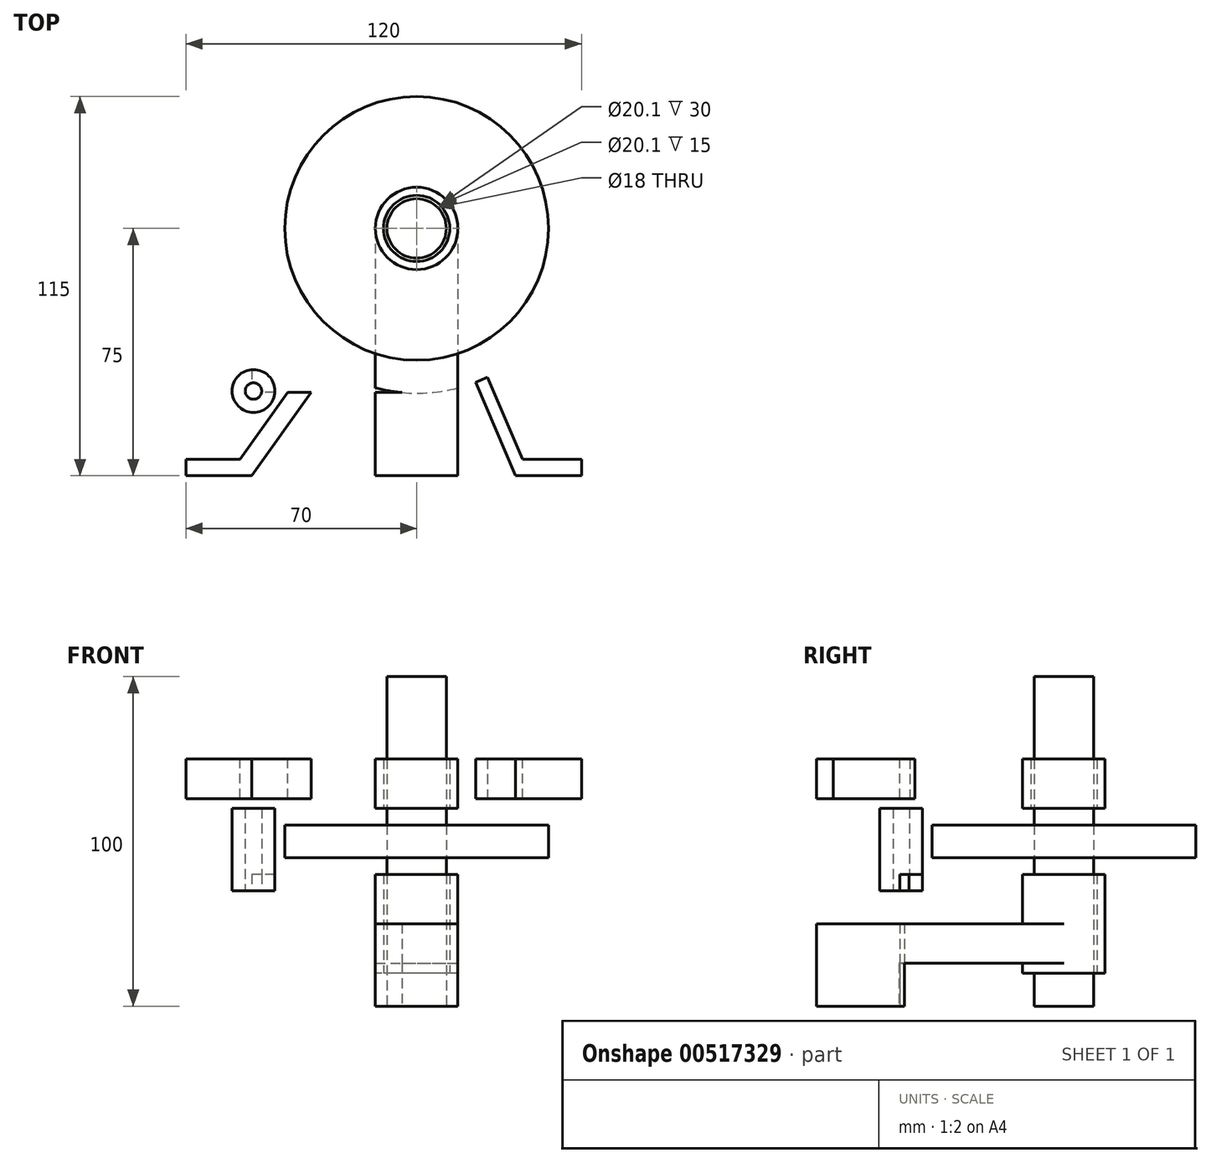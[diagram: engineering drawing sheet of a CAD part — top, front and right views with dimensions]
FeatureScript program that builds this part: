
annotation { "Feature Type Name" : "Feature", "Feature Type Description" : "" }
export const myFeature = defineFeature(function(context is Context, id is Id, definition is map)
    precondition{}
    {
        {
            var Q0;
            Q0=qCreatedBy(makeId("Top.planeOp"),FACE);
            var sketch = newSketch(context, id + "F0", { "sketchPlane" : qUnion([Q0])});
            skCircle(sketch, "E0", {"center": v(0, 0) * mm, "radius": 9 * mm});
            skCircle(sketch, "E1", {"center": v(0, 0) * mm, "radius": 10.05 * mm});
            skCircle(sketch, "E2", {"center": v(0, 0) * mm, "radius": 12.5 * mm});
            skCircle(sketch, "E3", {"center": v(0, 0) * mm, "radius": 50 * mm});
            skLineSegment(sketch, "E4", {"start": v(0, 0) * mm, "end": v(-35.84, -34.86) * mm});
            skLineSegment(sketch, "E5", {"start": v(0, 0) * mm, "end": v(0, 50) * mm});
            skCircle(sketch, "E6", {"center": v(0, 0) * mm, "radius": 45 * mm});
            skCircle(sketch, "E7", {"center": v(0, 0) * mm, "radius": 40 * mm});
            skLineSegment(sketch, "E8.bottom", {"start": v(-12.5, 75) * mm, "end": v(12.5, 75) * mm});
            skLineSegment(sketch, "E8.top", {"start": v(-12.5, -75) * mm, "end": v(12.5, -75) * mm});
            skLineSegment(sketch, "E8.left", {"start": v(-12.5, 75) * mm, "end": v(-12.5, -75) * mm});
            skLineSegment(sketch, "E8.right", {"start": v(12.5, 75) * mm, "end": v(12.5, -75) * mm});
            skLineSegment(sketch, "E9", {"start": v(-50, 0) * mm, "end": v(-50, -49.8) * mm});
            skLineSegment(sketch, "E10", {"start": v(-4.45, -49.8) * mm, "end": v(-50, -49.8) * mm});
            skSolve(sketch);
        }
        {
            var Q0;
            Q0=makeQuery(id+"F0.imprint","IMPRINT",FACE,{"disambiguationData":[TD([[makeQuery(id+"F0.imprint","IMPRINT",EDGE,{"derivedFrom":sQuery(id+"F0.wireOp",EDGE,"E0")}),1.0]])]});
            extrude(context, id + "F1", {"entities" : qUnion([Q0]), "depth" : 100 * mm, "offsetDistance" : 25 * mm});
        }
        {
            var Q0;
            {var subQ0=sQuery(id+"F0.wireOp",EDGE,"E4");var subQ1=sQuery(id+"F0.wireOp",EDGE,"E1");var subQ2=makeQuery(id+"F0.imprint","INTERSECT",VERTEX,{"derivedFrom":[subQ1,subQ0]});Q0=makeQuery(id+"F0.imprint","IMPRINT",FACE,{"disambiguationData":[TD([[makeQuery(id+"F0.imprint","IMPRINT",EDGE,{"disambiguationData":[TD([[subQ2,-1.0]])],"derivedFrom":subQ1}),-1.0]])]});}
            var Q1;
            {var subQ0=sQuery(id+"F0.wireOp",EDGE,"E4");var subQ1=sQuery(id+"F0.wireOp",EDGE,"E1");var subQ2=makeQuery(id+"F0.imprint","INTERSECT",VERTEX,{"derivedFrom":[subQ1,subQ0]});Q1=makeQuery(id+"F0.imprint","IMPRINT",FACE,{"disambiguationData":[TD([[makeQuery(id+"F0.imprint","IMPRINT",EDGE,{"disambiguationData":[TD([[subQ2,1.0]])],"derivedFrom":subQ1}),-1.0]])]});}
            extrude(context, id + "F2", {"entities" : qUnion([Q0, Q1]), "depth" : 40 * mm, "offsetDistance" : 25 * mm, "hasSecondDirection" : true, "secondDirectionOppositeDirection" : true, "secondDirectionDepth" : -10 * mm});
        }
        {
            var Q0;
            {var subQ0=sQuery(id+"F0.wireOp",EDGE,"E4");var subQ1=sQuery(id+"F0.wireOp",EDGE,"E1");var subQ2=makeQuery(id+"F0.imprint","INTERSECT",VERTEX,{"derivedFrom":[subQ1,subQ0]});Q0=makeQuery(id+"F0.imprint","IMPRINT",FACE,{"disambiguationData":[TD([[makeQuery(id+"F0.imprint","IMPRINT",EDGE,{"disambiguationData":[TD([[subQ2,-1.0]])],"derivedFrom":subQ1}),-1.0]])]});}
            var Q1;
            {var subQ0=sQuery(id+"F0.wireOp",EDGE,"E4");var subQ1=sQuery(id+"F0.wireOp",EDGE,"E1");var subQ2=makeQuery(id+"F0.imprint","INTERSECT",VERTEX,{"derivedFrom":[subQ1,subQ0]});Q1=makeQuery(id+"F0.imprint","IMPRINT",FACE,{"disambiguationData":[TD([[makeQuery(id+"F0.imprint","IMPRINT",EDGE,{"disambiguationData":[TD([[subQ2,1.0]])],"derivedFrom":subQ1}),-1.0]])]});}
            extrude(context, id + "F3", {"entities" : qUnion([Q0, Q1]), "depth" : 75 * mm, "offsetDistance" : 25 * mm, "hasSecondDirection" : true, "secondDirectionOppositeDirection" : true, "secondDirectionDepth" : -60 * mm});
        }
        {
            var Q0;
            {var subQ0=sQuery(id+"F0.wireOp",EDGE,"E4");var subQ1=sQuery(id+"F0.wireOp",EDGE,"E2");var subQ2=makeQuery(id+"F0.imprint","INTERSECT",VERTEX,{"derivedFrom":[subQ1,subQ0]});Q0=makeQuery(id+"F0.imprint","IMPRINT",FACE,{"disambiguationData":[TD([[makeQuery(id+"F0.imprint","IMPRINT",EDGE,{"disambiguationData":[TD([[subQ2,-1.0]])],"derivedFrom":subQ1}),-1.0]])]});}
            var Q1;
            {var subQ0=sQuery(id+"F0.wireOp",EDGE,"E4");var subQ1=sQuery(id+"F0.wireOp",EDGE,"E3");var subQ2=makeQuery(id+"F0.imprint","INTERSECT",VERTEX,{"derivedFrom":[subQ1,subQ0]});Q1=makeQuery(id+"F0.imprint","IMPRINT",FACE,{"disambiguationData":[TD([[makeQuery(id+"F0.imprint","IMPRINT",EDGE,{"disambiguationData":[TD([[subQ2,-1.0]])],"derivedFrom":subQ1}),1.0]])]});}
            var Q2;
            {var subQ0=sQuery(id+"F0.wireOp",EDGE,"E7");var subQ1=sQuery(id+"F0.wireOp",EDGE,"E4");var subQ2=makeQuery(id+"F0.imprint","INTERSECT",VERTEX,{"derivedFrom":[subQ1,subQ0]});Q2=makeQuery(id+"F0.imprint","IMPRINT",FACE,{"disambiguationData":[TD([[makeQuery(id+"F0.imprint","IMPRINT",EDGE,{"disambiguationData":[TD([[subQ2,-1.0]])],"derivedFrom":subQ1}),1.0]])]});}
            var Q3;
            {var subQ0=sQuery(id+"F0.wireOp",EDGE,"E7");var subQ1=sQuery(id+"F0.wireOp",EDGE,"E5");var subQ2=makeQuery(id+"F0.imprint","INTERSECT",VERTEX,{"derivedFrom":[subQ1,subQ0]});Q3=makeQuery(id+"F0.imprint","IMPRINT",FACE,{"disambiguationData":[TD([[makeQuery(id+"F0.imprint","IMPRINT",EDGE,{"disambiguationData":[TD([[subQ2,-1.0]])],"derivedFrom":subQ1}),-1.0]])]});}
            var Q4;
            {var subQ0=sQuery(id+"F0.wireOp",EDGE,"E5");var subQ1=sQuery(id+"F0.wireOp",EDGE,"E3");var subQ2=makeQuery(id+"F0.imprint","INTERSECT",VERTEX,{"derivedFrom":[subQ1,subQ0]});Q4=makeQuery(id+"F0.imprint","IMPRINT",FACE,{"disambiguationData":[TD([[makeQuery(id+"F0.imprint","IMPRINT",EDGE,{"disambiguationData":[TD([[subQ2,1.0]])],"derivedFrom":subQ1}),1.0]])]});}
            var Q5;
            {var subQ0=sQuery(id+"F0.wireOp",EDGE,"E8.right");var subQ1=sQuery(id+"F0.wireOp",EDGE,"E3");var subQ2=makeQuery(id+"F0.imprint","INTERSECT",VERTEX,{"disambiguationData":[OD(0.0)],"derivedFrom":[subQ1,subQ0]});Q5=makeQuery(id+"F0.imprint","IMPRINT",FACE,{"disambiguationData":[TD([[makeQuery(id+"F0.imprint","IMPRINT",EDGE,{"disambiguationData":[TD([[subQ2,1.0]])],"derivedFrom":subQ1}),1.0]])]});}
            var Q6;
            {var subQ0=sQuery(id+"F0.wireOp",EDGE,"E8.right");var subQ1=sQuery(id+"F0.wireOp",EDGE,"E6");var subQ2=makeQuery(id+"F0.imprint","INTERSECT",VERTEX,{"disambiguationData":[OD(0.0)],"derivedFrom":[subQ1,subQ0]});Q6=makeQuery(id+"F0.imprint","IMPRINT",FACE,{"disambiguationData":[TD([[makeQuery(id+"F0.imprint","IMPRINT",EDGE,{"disambiguationData":[TD([[subQ2,1.0]])],"derivedFrom":subQ1}),1.0]])]});}
            var Q7;
            {var subQ0=sQuery(id+"F0.wireOp",EDGE,"E8.left");var subQ1=sQuery(id+"F0.wireOp",EDGE,"E6");var subQ2=makeQuery(id+"F0.imprint","INTERSECT",VERTEX,{"disambiguationData":[OD(1.0)],"derivedFrom":[subQ1,subQ0]});Q7=makeQuery(id+"F0.imprint","IMPRINT",FACE,{"disambiguationData":[TD([[makeQuery(id+"F0.imprint","IMPRINT",EDGE,{"disambiguationData":[TD([[subQ2,-1.0]])],"derivedFrom":subQ1}),1.0]])]});}
            var Q8;
            {var subQ0=sQuery(id+"F0.wireOp",EDGE,"E8.left");var subQ1=sQuery(id+"F0.wireOp",EDGE,"E3");var subQ2=makeQuery(id+"F0.imprint","INTERSECT",VERTEX,{"disambiguationData":[OD(1.0)],"derivedFrom":[subQ1,subQ0]});Q8=makeQuery(id+"F0.imprint","IMPRINT",FACE,{"disambiguationData":[TD([[makeQuery(id+"F0.imprint","IMPRINT",EDGE,{"disambiguationData":[TD([[subQ2,-1.0]])],"derivedFrom":subQ1}),1.0]])]});}
            var Q9;
            {var subQ0=sQuery(id+"F0.wireOp",EDGE,"E8.right");var subQ1=sQuery(id+"F0.wireOp",EDGE,"E7");var subQ2=makeQuery(id+"F0.imprint","INTERSECT",VERTEX,{"disambiguationData":[OD(0.0)],"derivedFrom":[subQ1,subQ0]});Q9=makeQuery(id+"F0.imprint","IMPRINT",FACE,{"disambiguationData":[TD([[makeQuery(id+"F0.imprint","IMPRINT",EDGE,{"disambiguationData":[TD([[subQ2,1.0]])],"derivedFrom":subQ1}),1.0]])]});}
            var Q10;
            {var subQ0=sQuery(id+"F0.wireOp",EDGE,"E5");var subQ1=sQuery(id+"F0.wireOp",EDGE,"E2");var subQ2=makeQuery(id+"F0.imprint","INTERSECT",VERTEX,{"derivedFrom":[subQ1,subQ0]});Q10=makeQuery(id+"F0.imprint","IMPRINT",FACE,{"disambiguationData":[TD([[makeQuery(id+"F0.imprint","IMPRINT",EDGE,{"disambiguationData":[TD([[subQ2,1.0]])],"derivedFrom":subQ1}),-1.0]])]});}
            var Q11;
            {var subQ0=sQuery(id+"F0.wireOp",EDGE,"E8.left");var subQ1=sQuery(id+"F0.wireOp",EDGE,"E4");var subQ2=makeQuery(id+"F0.imprint","INTERSECT",VERTEX,{"derivedFrom":[subQ1,subQ0]});Q11=makeQuery(id+"F0.imprint","IMPRINT",FACE,{"disambiguationData":[TD([[makeQuery(id+"F0.imprint","IMPRINT",EDGE,{"disambiguationData":[TD([[subQ2,-1.0]])],"derivedFrom":subQ1}),1.0]])]});}
            var Q12;
            {var subQ0=sQuery(id+"F0.wireOp",EDGE,"E5");var subQ1=sQuery(id+"F0.wireOp",EDGE,"E2");var subQ2=makeQuery(id+"F0.imprint","INTERSECT",VERTEX,{"derivedFrom":[subQ1,subQ0]});Q12=makeQuery(id+"F0.imprint","IMPRINT",FACE,{"disambiguationData":[TD([[makeQuery(id+"F0.imprint","IMPRINT",EDGE,{"disambiguationData":[TD([[subQ2,-1.0]])],"derivedFrom":subQ1}),-1.0]])]});}
            var Q13;
            {var subQ0=sQuery(id+"F0.wireOp",EDGE,"E8.left");var subQ1=sQuery(id+"F0.wireOp",EDGE,"E4");var subQ2=makeQuery(id+"F0.imprint","INTERSECT",VERTEX,{"derivedFrom":[subQ1,subQ0]});Q13=makeQuery(id+"F0.imprint","IMPRINT",FACE,{"disambiguationData":[TD([[makeQuery(id+"F0.imprint","IMPRINT",EDGE,{"disambiguationData":[TD([[subQ2,-1.0]])],"derivedFrom":subQ1}),-1.0]])]});}
            var Q14;
            {var subQ0=sQuery(id+"F0.wireOp",EDGE,"E8.left");var subQ1=sQuery(id+"F0.wireOp",EDGE,"E2");var subQ2=makeQuery(id+"F0.imprint","INTERSECT",VERTEX,{"derivedFrom":[subQ1,subQ0]});Q14=makeQuery(id+"F0.imprint","IMPRINT",FACE,{"disambiguationData":[TD([[makeQuery(id+"F0.imprint","IMPRINT",EDGE,{"disambiguationData":[TD([[subQ2,-1.0]])],"derivedFrom":subQ1}),-1.0]])]});}
            var Q15;
            {var subQ0=sQuery(id+"F0.wireOp",EDGE,"E7");var subQ1=sQuery(id+"F0.wireOp",EDGE,"E4");var subQ2=makeQuery(id+"F0.imprint","INTERSECT",VERTEX,{"derivedFrom":[subQ1,subQ0]});Q15=makeQuery(id+"F0.imprint","IMPRINT",FACE,{"disambiguationData":[TD([[makeQuery(id+"F0.imprint","IMPRINT",EDGE,{"disambiguationData":[TD([[subQ2,-1.0]])],"derivedFrom":subQ1}),-1.0]])]});}
            var Q16;
            {var subQ0=sQuery(id+"F0.wireOp",EDGE,"E4");var subQ1=sQuery(id+"F0.wireOp",EDGE,"E3");var subQ2=makeQuery(id+"F0.imprint","INTERSECT",VERTEX,{"derivedFrom":[subQ1,subQ0]});Q16=makeQuery(id+"F0.imprint","IMPRINT",FACE,{"disambiguationData":[TD([[makeQuery(id+"F0.imprint","IMPRINT",EDGE,{"disambiguationData":[TD([[subQ2,1.0]])],"derivedFrom":subQ1}),1.0]])]});}
            var Q17;
            {var subQ0=sQuery(id+"F0.wireOp",EDGE,"E7");var subQ1=sQuery(id+"F0.wireOp",EDGE,"E5");var subQ2=makeQuery(id+"F0.imprint","INTERSECT",VERTEX,{"derivedFrom":[subQ1,subQ0]});Q17=makeQuery(id+"F0.imprint","IMPRINT",FACE,{"disambiguationData":[TD([[makeQuery(id+"F0.imprint","IMPRINT",EDGE,{"disambiguationData":[TD([[subQ2,-1.0]])],"derivedFrom":subQ1}),1.0]])]});}
            var Q18;
            {var subQ0=sQuery(id+"F0.wireOp",EDGE,"E5");var subQ1=sQuery(id+"F0.wireOp",EDGE,"E3");var subQ2=makeQuery(id+"F0.imprint","INTERSECT",VERTEX,{"derivedFrom":[subQ1,subQ0]});Q18=makeQuery(id+"F0.imprint","IMPRINT",FACE,{"disambiguationData":[TD([[makeQuery(id+"F0.imprint","IMPRINT",EDGE,{"disambiguationData":[TD([[subQ2,-1.0]])],"derivedFrom":subQ1}),1.0]])]});}
            var Q19;
            {var subQ0=sQuery(id+"F0.wireOp",EDGE,"FEy6LhcJ-vW1g-UwPa-rVGF-p8I0dYB5r2JZ");var subQ1=sQuery(id+"F0.wireOp",EDGE,"E3");var subQ2=makeQuery(id+"F0.imprint","INTERSECT",VERTEX,{"derivedFrom":[subQ1,subQ0]});Q19=makeQuery(id+"F0.imprint","IMPRINT",FACE,{"disambiguationData":[TD([[makeQuery(id+"F0.imprint","IMPRINT",EDGE,{"disambiguationData":[TD([[subQ2,1.0]])],"derivedFrom":subQ1}),-1.0]])]});}
            var Q20;
            {var subQ0=sQuery(id+"F0.wireOp",EDGE,"E9");Q20=makeQuery(id+"F0.imprint","IMPRINT",FACE,{"disambiguationData":[TD([[makeQuery(id+"F0.imprint","IMPRINT",EDGE,{"derivedFrom":subQ0}),1.0]])]});}
            extrude(context, id + "F4", {"entities" : qUnion([Q0, Q1, Q2, Q3, Q4, Q5, Q6, Q7, Q8, Q9, Q10, Q11, Q12, Q13, Q14, Q15, Q16, Q17, Q18, Q19, Q20]), "operationType" : NewBodyOperationType.ADD, "depth" : 40 * mm, "offsetDistance" : 25 * mm, "hasSecondDirection" : true, "secondDirectionOppositeDirection" : true, "secondDirectionDepth" : -35 * mm});
        }
        {
            var Q0;
            {var subQ0=sQuery(id+"F0.wireOp",EDGE,"E4");var subQ1=sQuery(id+"F0.wireOp",EDGE,"E3");var subQ2=makeQuery(id+"F0.imprint","INTERSECT",VERTEX,{"derivedFrom":[subQ1,subQ0]});Q0=makeQuery(id+"F0.imprint","IMPRINT",FACE,{"disambiguationData":[TD([[makeQuery(id+"F0.imprint","IMPRINT",EDGE,{"disambiguationData":[TD([[subQ2,-1.0]])],"derivedFrom":subQ1}),1.0]])]});}
            var Q1;
            {var subQ0=sQuery(id+"F0.wireOp",EDGE,"E8.left");var subQ1=sQuery(id+"F0.wireOp",EDGE,"E3");var subQ2=makeQuery(id+"F0.imprint","INTERSECT",VERTEX,{"disambiguationData":[OD(1.0)],"derivedFrom":[subQ1,subQ0]});Q1=makeQuery(id+"F0.imprint","IMPRINT",FACE,{"disambiguationData":[TD([[makeQuery(id+"F0.imprint","IMPRINT",EDGE,{"disambiguationData":[TD([[subQ2,-1.0]])],"derivedFrom":subQ1}),1.0]])]});}
            var Q2;
            {var subQ0=sQuery(id+"F0.wireOp",EDGE,"E8.right");var subQ1=sQuery(id+"F0.wireOp",EDGE,"E3");var subQ2=makeQuery(id+"F0.imprint","INTERSECT",VERTEX,{"disambiguationData":[OD(0.0)],"derivedFrom":[subQ1,subQ0]});Q2=makeQuery(id+"F0.imprint","IMPRINT",FACE,{"disambiguationData":[TD([[makeQuery(id+"F0.imprint","IMPRINT",EDGE,{"disambiguationData":[TD([[subQ2,1.0]])],"derivedFrom":subQ1}),1.0]])]});}
            var Q3;
            {var subQ0=sQuery(id+"F0.wireOp",EDGE,"E5");var subQ1=sQuery(id+"F0.wireOp",EDGE,"E3");var subQ2=makeQuery(id+"F0.imprint","INTERSECT",VERTEX,{"derivedFrom":[subQ1,subQ0]});Q3=makeQuery(id+"F0.imprint","IMPRINT",FACE,{"disambiguationData":[TD([[makeQuery(id+"F0.imprint","IMPRINT",EDGE,{"disambiguationData":[TD([[subQ2,1.0]])],"derivedFrom":subQ1}),1.0]])]});}
            extrude(context, id + "F5", {"entities" : qUnion([Q0, Q1, Q2, Q3]), "operationType" : NewBodyOperationType.ADD, "depth" : 60 * mm, "offsetDistance" : 25 * mm, "hasSecondDirection" : true, "secondDirectionOppositeDirection" : true, "secondDirectionDepth" : -40 * mm});
        }
        {
            var Q0;
            {var subQ0=sQuery(id+"F0.wireOp",EDGE,"E8.right");var subQ1=sQuery(id+"F0.wireOp",EDGE,"E7");var subQ2=makeQuery(id+"F0.imprint","INTERSECT",VERTEX,{"disambiguationData":[OD(0.0)],"derivedFrom":[subQ1,subQ0]});Q0=makeQuery(id+"F0.imprint","IMPRINT",FACE,{"disambiguationData":[TD([[makeQuery(id+"F0.imprint","IMPRINT",EDGE,{"disambiguationData":[TD([[subQ2,1.0]])],"derivedFrom":subQ1}),1.0]])]});}
            var Q1;
            {var subQ0=sQuery(id+"F0.wireOp",EDGE,"E8.right");var subQ1=sQuery(id+"F0.wireOp",EDGE,"E6");var subQ2=makeQuery(id+"F0.imprint","INTERSECT",VERTEX,{"disambiguationData":[OD(0.0)],"derivedFrom":[subQ1,subQ0]});Q1=makeQuery(id+"F0.imprint","IMPRINT",FACE,{"disambiguationData":[TD([[makeQuery(id+"F0.imprint","IMPRINT",EDGE,{"disambiguationData":[TD([[subQ2,1.0]])],"derivedFrom":subQ1}),1.0]])]});}
            var Q2;
            {var subQ0=sQuery(id+"F0.wireOp",EDGE,"E8.right");var subQ1=sQuery(id+"F0.wireOp",EDGE,"E3");var subQ2=makeQuery(id+"F0.imprint","INTERSECT",VERTEX,{"disambiguationData":[OD(0.0)],"derivedFrom":[subQ1,subQ0]});Q2=makeQuery(id+"F0.imprint","IMPRINT",FACE,{"disambiguationData":[TD([[makeQuery(id+"F0.imprint","IMPRINT",EDGE,{"disambiguationData":[TD([[subQ2,1.0]])],"derivedFrom":subQ1}),1.0]])]});}
            var Q3;
            {var subQ0=sQuery(id+"F0.wireOp",EDGE,"E5");var subQ1=sQuery(id+"F0.wireOp",EDGE,"E3");var subQ2=makeQuery(id+"F0.imprint","INTERSECT",VERTEX,{"derivedFrom":[subQ1,subQ0]});Q3=makeQuery(id+"F0.imprint","IMPRINT",FACE,{"disambiguationData":[TD([[makeQuery(id+"F0.imprint","IMPRINT",EDGE,{"disambiguationData":[TD([[subQ2,1.0]])],"derivedFrom":subQ1}),1.0]])]});}
            var Q4;
            {var subQ0=sQuery(id+"F0.wireOp",EDGE,"E5");var subQ1=sQuery(id+"F0.wireOp",EDGE,"E2");var subQ2=makeQuery(id+"F0.imprint","INTERSECT",VERTEX,{"derivedFrom":[subQ1,subQ0]});Q4=makeQuery(id+"F0.imprint","IMPRINT",FACE,{"disambiguationData":[TD([[makeQuery(id+"F0.imprint","IMPRINT",EDGE,{"disambiguationData":[TD([[subQ2,1.0]])],"derivedFrom":subQ1}),-1.0]])]});}
            var Q5;
            {var subQ0=sQuery(id+"F0.wireOp",EDGE,"E7");var subQ1=sQuery(id+"F0.wireOp",EDGE,"E5");var subQ2=makeQuery(id+"F0.imprint","INTERSECT",VERTEX,{"derivedFrom":[subQ1,subQ0]});Q5=makeQuery(id+"F0.imprint","IMPRINT",FACE,{"disambiguationData":[TD([[makeQuery(id+"F0.imprint","IMPRINT",EDGE,{"disambiguationData":[TD([[subQ2,-1.0]])],"derivedFrom":subQ1}),-1.0]])]});}
            var Q6;
            {var subQ0=sQuery(id+"F0.wireOp",EDGE,"E5");var subQ1=sQuery(id+"F0.wireOp",EDGE,"E3");var subQ2=makeQuery(id+"F0.imprint","INTERSECT",VERTEX,{"derivedFrom":[subQ1,subQ0]});Q6=makeQuery(id+"F0.imprint","IMPRINT",FACE,{"disambiguationData":[TD([[makeQuery(id+"F0.imprint","IMPRINT",EDGE,{"disambiguationData":[TD([[subQ2,-1.0]])],"derivedFrom":subQ1}),1.0]])]});}
            var Q7;
            {var subQ0=sQuery(id+"F0.wireOp",EDGE,"E7");var subQ1=sQuery(id+"F0.wireOp",EDGE,"E5");var subQ2=makeQuery(id+"F0.imprint","INTERSECT",VERTEX,{"derivedFrom":[subQ1,subQ0]});Q7=makeQuery(id+"F0.imprint","IMPRINT",FACE,{"disambiguationData":[TD([[makeQuery(id+"F0.imprint","IMPRINT",EDGE,{"disambiguationData":[TD([[subQ2,-1.0]])],"derivedFrom":subQ1}),1.0]])]});}
            var Q8;
            {var subQ0=sQuery(id+"F0.wireOp",EDGE,"E5");var subQ1=sQuery(id+"F0.wireOp",EDGE,"E2");var subQ2=makeQuery(id+"F0.imprint","INTERSECT",VERTEX,{"derivedFrom":[subQ1,subQ0]});Q8=makeQuery(id+"F0.imprint","IMPRINT",FACE,{"disambiguationData":[TD([[makeQuery(id+"F0.imprint","IMPRINT",EDGE,{"disambiguationData":[TD([[subQ2,-1.0]])],"derivedFrom":subQ1}),-1.0]])]});}
            var Q9;
            {var subQ5=sQuery(id+"F0.wireOp",EDGE,"E8.right");var subQ7=sQuery(id+"F0.wireOp",EDGE,"E2");var subQ9=makeQuery(id+"F0.imprint","INTERSECT",VERTEX,{"derivedFrom":[subQ7,subQ5]});Q9=makeQuery(id+"F0.imprint","IMPRINT",FACE,{"disambiguationData":[TD([[makeQuery(id+"F0.imprint","IMPRINT",EDGE,{"disambiguationData":[TD([[subQ9,1.0]])],"derivedFrom":subQ7}),-1.0]])]});}
            var Q10;
            {var subQ0=sQuery(id+"F0.wireOp",EDGE,"E8.left");var subQ1=sQuery(id+"F0.wireOp",EDGE,"E4");var subQ2=makeQuery(id+"F0.imprint","INTERSECT",VERTEX,{"derivedFrom":[subQ1,subQ0]});Q10=makeQuery(id+"F0.imprint","IMPRINT",FACE,{"disambiguationData":[TD([[makeQuery(id+"F0.imprint","IMPRINT",EDGE,{"disambiguationData":[TD([[subQ2,-1.0]])],"derivedFrom":subQ1}),-1.0]])]});}
            var Q11;
            {var subQ0=sQuery(id+"F0.wireOp",EDGE,"E8.left");var subQ1=sQuery(id+"F0.wireOp",EDGE,"E4");var subQ2=makeQuery(id+"F0.imprint","INTERSECT",VERTEX,{"derivedFrom":[subQ1,subQ0]});Q11=makeQuery(id+"F0.imprint","IMPRINT",FACE,{"disambiguationData":[TD([[makeQuery(id+"F0.imprint","IMPRINT",EDGE,{"disambiguationData":[TD([[subQ2,-1.0]])],"derivedFrom":subQ1}),1.0]])]});}
            var Q12;
            {var subQ0=sQuery(id+"F0.wireOp",EDGE,"E7");var subQ1=sQuery(id+"F0.wireOp",EDGE,"E4");var subQ2=makeQuery(id+"F0.imprint","INTERSECT",VERTEX,{"derivedFrom":[subQ1,subQ0]});Q12=makeQuery(id+"F0.imprint","IMPRINT",FACE,{"disambiguationData":[TD([[makeQuery(id+"F0.imprint","IMPRINT",EDGE,{"disambiguationData":[TD([[subQ2,-1.0]])],"derivedFrom":subQ1}),1.0]])]});}
            var Q13;
            {var subQ0=sQuery(id+"F0.wireOp",EDGE,"E4");var subQ1=sQuery(id+"F0.wireOp",EDGE,"E3");var subQ2=makeQuery(id+"F0.imprint","INTERSECT",VERTEX,{"derivedFrom":[subQ1,subQ0]});Q13=makeQuery(id+"F0.imprint","IMPRINT",FACE,{"disambiguationData":[TD([[makeQuery(id+"F0.imprint","IMPRINT",EDGE,{"disambiguationData":[TD([[subQ2,-1.0]])],"derivedFrom":subQ1}),1.0]])]});}
            var Q14;
            {var subQ0=sQuery(id+"F0.wireOp",EDGE,"E8.left");var subQ1=sQuery(id+"F0.wireOp",EDGE,"E6");var subQ2=makeQuery(id+"F0.imprint","INTERSECT",VERTEX,{"disambiguationData":[OD(1.0)],"derivedFrom":[subQ1,subQ0]});Q14=makeQuery(id+"F0.imprint","IMPRINT",FACE,{"disambiguationData":[TD([[makeQuery(id+"F0.imprint","IMPRINT",EDGE,{"disambiguationData":[TD([[subQ2,-1.0]])],"derivedFrom":subQ1}),1.0]])]});}
            var Q15;
            {var subQ0=sQuery(id+"F0.wireOp",EDGE,"E8.left");var subQ1=sQuery(id+"F0.wireOp",EDGE,"E3");var subQ2=makeQuery(id+"F0.imprint","INTERSECT",VERTEX,{"disambiguationData":[OD(1.0)],"derivedFrom":[subQ1,subQ0]});Q15=makeQuery(id+"F0.imprint","IMPRINT",FACE,{"disambiguationData":[TD([[makeQuery(id+"F0.imprint","IMPRINT",EDGE,{"disambiguationData":[TD([[subQ2,-1.0]])],"derivedFrom":subQ1}),1.0]])]});}
            var Q16;
            {var subQ0=sQuery(id+"F0.wireOp",EDGE,"E7");var subQ1=sQuery(id+"F0.wireOp",EDGE,"E4");var subQ2=makeQuery(id+"F0.imprint","INTERSECT",VERTEX,{"derivedFrom":[subQ1,subQ0]});Q16=makeQuery(id+"F0.imprint","IMPRINT",FACE,{"disambiguationData":[TD([[makeQuery(id+"F0.imprint","IMPRINT",EDGE,{"disambiguationData":[TD([[subQ2,-1.0]])],"derivedFrom":subQ1}),-1.0]])]});}
            var Q17;
            {var subQ0=sQuery(id+"F0.wireOp",EDGE,"E4");var subQ1=sQuery(id+"F0.wireOp",EDGE,"E3");var subQ2=makeQuery(id+"F0.imprint","INTERSECT",VERTEX,{"derivedFrom":[subQ1,subQ0]});Q17=makeQuery(id+"F0.imprint","IMPRINT",FACE,{"disambiguationData":[TD([[makeQuery(id+"F0.imprint","IMPRINT",EDGE,{"disambiguationData":[TD([[subQ2,1.0]])],"derivedFrom":subQ1}),1.0]])]});}
            var Q18;
            {var subQ0=sQuery(id+"F0.wireOp",EDGE,"E8.left");var subQ1=sQuery(id+"F0.wireOp",EDGE,"E2");var subQ2=makeQuery(id+"F0.imprint","INTERSECT",VERTEX,{"derivedFrom":[subQ1,subQ0]});Q18=makeQuery(id+"F0.imprint","IMPRINT",FACE,{"disambiguationData":[TD([[makeQuery(id+"F0.imprint","IMPRINT",EDGE,{"disambiguationData":[TD([[subQ2,-1.0]])],"derivedFrom":subQ1}),-1.0]])]});}
            extrude(context, id + "F6", {"entities" : qUnion([Q0, Q1, Q2, Q3, Q4, Q5, Q6, Q7, Q8, Q9, Q10, Q11, Q12, Q13, Q14, Q15, Q16, Q17, Q18]), "operationType" : NewBodyOperationType.ADD, "depth" : 65 * mm, "offsetDistance" : 25 * mm, "hasSecondDirection" : true, "secondDirectionOppositeDirection" : true, "secondDirectionDepth" : -60 * mm});
        }
        {
            var Q0;
            {var subQ0=sQuery(id+"F0.wireOp",EDGE,"E8.left");var subQ1=sQuery(id+"F0.wireOp",EDGE,"E4");var subQ2=makeQuery(id+"F0.imprint","INTERSECT",VERTEX,{"derivedFrom":[subQ1,subQ0]});Q0=makeQuery(id+"F0.imprint","IMPRINT",FACE,{"disambiguationData":[TD([[makeQuery(id+"F0.imprint","IMPRINT",EDGE,{"disambiguationData":[TD([[subQ2,-1.0]])],"derivedFrom":subQ1}),-1.0]])]});}
            var Q1;
            {var subQ0=sQuery(id+"F0.wireOp",EDGE,"E5");var subQ1=sQuery(id+"F0.wireOp",EDGE,"E2");var subQ2=makeQuery(id+"F0.imprint","INTERSECT",VERTEX,{"derivedFrom":[subQ1,subQ0]});Q1=makeQuery(id+"F0.imprint","IMPRINT",FACE,{"disambiguationData":[TD([[makeQuery(id+"F0.imprint","IMPRINT",EDGE,{"disambiguationData":[TD([[subQ2,-1.0]])],"derivedFrom":subQ1}),-1.0]])]});}
            var Q2;
            {var subQ0=sQuery(id+"F0.wireOp",EDGE,"E5");var subQ1=sQuery(id+"F0.wireOp",EDGE,"E2");var subQ2=makeQuery(id+"F0.imprint","INTERSECT",VERTEX,{"derivedFrom":[subQ1,subQ0]});Q2=makeQuery(id+"F0.imprint","IMPRINT",FACE,{"disambiguationData":[TD([[makeQuery(id+"F0.imprint","IMPRINT",EDGE,{"disambiguationData":[TD([[subQ2,1.0]])],"derivedFrom":subQ1}),-1.0]])]});}
            var Q3;
            {var subQ0=sQuery(id+"F0.wireOp",EDGE,"E8.right");var subQ1=sQuery(id+"F0.wireOp",EDGE,"E7");var subQ2=makeQuery(id+"F0.imprint","INTERSECT",VERTEX,{"disambiguationData":[OD(0.0)],"derivedFrom":[subQ1,subQ0]});Q3=makeQuery(id+"F0.imprint","IMPRINT",FACE,{"disambiguationData":[TD([[makeQuery(id+"F0.imprint","IMPRINT",EDGE,{"disambiguationData":[TD([[subQ2,1.0]])],"derivedFrom":subQ1}),1.0]])]});}
            var Q4;
            {var subQ0=sQuery(id+"F0.wireOp",EDGE,"E8.left");var subQ1=sQuery(id+"F0.wireOp",EDGE,"E4");var subQ2=makeQuery(id+"F0.imprint","INTERSECT",VERTEX,{"derivedFrom":[subQ1,subQ0]});Q4=makeQuery(id+"F0.imprint","IMPRINT",FACE,{"disambiguationData":[TD([[makeQuery(id+"F0.imprint","IMPRINT",EDGE,{"disambiguationData":[TD([[subQ2,-1.0]])],"derivedFrom":subQ1}),1.0]])]});}
            var Q5;
            {var subQ5=sQuery(id+"F0.wireOp",EDGE,"E8.right");var subQ7=sQuery(id+"F0.wireOp",EDGE,"E2");var subQ9=makeQuery(id+"F0.imprint","INTERSECT",VERTEX,{"derivedFrom":[subQ7,subQ5]});Q5=makeQuery(id+"F0.imprint","IMPRINT",FACE,{"disambiguationData":[TD([[makeQuery(id+"F0.imprint","IMPRINT",EDGE,{"disambiguationData":[TD([[subQ9,1.0]])],"derivedFrom":subQ7}),-1.0]])]});}
            var Q6;
            {var subQ0=sQuery(id+"F0.wireOp",EDGE,"E8.left");var subQ1=sQuery(id+"F0.wireOp",EDGE,"E2");var subQ2=makeQuery(id+"F0.imprint","INTERSECT",VERTEX,{"derivedFrom":[subQ1,subQ0]});Q6=makeQuery(id+"F0.imprint","IMPRINT",FACE,{"disambiguationData":[TD([[makeQuery(id+"F0.imprint","IMPRINT",EDGE,{"disambiguationData":[TD([[subQ2,-1.0]])],"derivedFrom":subQ1}),-1.0]])]});}
            var Q7;
            {var subQ0=sQuery(id+"F0.wireOp",EDGE,"E4");var subQ1=sQuery(id+"F0.wireOp",EDGE,"E1");var subQ2=makeQuery(id+"F0.imprint","INTERSECT",VERTEX,{"derivedFrom":[subQ1,subQ0]});Q7=makeQuery(id+"F0.imprint","IMPRINT",FACE,{"disambiguationData":[TD([[makeQuery(id+"F0.imprint","IMPRINT",EDGE,{"disambiguationData":[TD([[subQ2,1.0]])],"derivedFrom":subQ1}),-1.0]])]});}
            var Q8;
            {var subQ0=sQuery(id+"F0.wireOp",EDGE,"E4");var subQ1=sQuery(id+"F0.wireOp",EDGE,"E1");var subQ2=makeQuery(id+"F0.imprint","INTERSECT",VERTEX,{"derivedFrom":[subQ1,subQ0]});Q8=makeQuery(id+"F0.imprint","IMPRINT",FACE,{"disambiguationData":[TD([[makeQuery(id+"F0.imprint","IMPRINT",EDGE,{"disambiguationData":[TD([[subQ2,-1.0]])],"derivedFrom":subQ1}),-1.0]])]});}
            var Q9;
            {var subQ0=sQuery(id+"F0.wireOp",EDGE,"E4");var subQ1=sQuery(id+"F0.wireOp",EDGE,"E0");var subQ2=makeQuery(id+"F0.imprint","INTERSECT",VERTEX,{"derivedFrom":[subQ1,subQ0]});Q9=makeQuery(id+"F0.imprint","IMPRINT",FACE,{"disambiguationData":[TD([[makeQuery(id+"F0.imprint","IMPRINT",EDGE,{"disambiguationData":[TD([[subQ2,1.0]])],"derivedFrom":subQ1}),-1.0]])]});}
            var Q10;
            {var subQ0=sQuery(id+"F0.wireOp",EDGE,"E4");var subQ1=sQuery(id+"F0.wireOp",EDGE,"E0");var subQ2=makeQuery(id+"F0.imprint","INTERSECT",VERTEX,{"derivedFrom":[subQ1,subQ0]});Q10=makeQuery(id+"F0.imprint","IMPRINT",FACE,{"disambiguationData":[TD([[makeQuery(id+"F0.imprint","IMPRINT",EDGE,{"disambiguationData":[TD([[subQ2,-1.0]])],"derivedFrom":subQ1}),-1.0]])]});}
            extrude(context, id + "F7", {"entities" : qUnion([Q0, Q1, Q2, Q3, Q4, Q5, Q6, Q7, Q8, Q9, Q10]), "depth" : 55 * mm, "offsetDistance" : 25 * mm, "hasSecondDirection" : true, "secondDirectionOppositeDirection" : true, "secondDirectionDepth" : -45 * mm});
        }
        {
            var Q0;
            {var subQ0=sQuery(id+"F0.wireOp",EDGE,"E4");var subQ1=sQuery(id+"F0.wireOp",EDGE,"E1");var subQ2=makeQuery(id+"F0.imprint","INTERSECT",VERTEX,{"derivedFrom":[subQ1,subQ0]});Q0=makeQuery(id+"F0.imprint","IMPRINT",FACE,{"disambiguationData":[TD([[makeQuery(id+"F0.imprint","IMPRINT",EDGE,{"disambiguationData":[TD([[subQ2,1.0]])],"derivedFrom":subQ1}),-1.0]])]});}
            var Q1;
            {var subQ0=sQuery(id+"F0.wireOp",EDGE,"E4");var subQ1=sQuery(id+"F0.wireOp",EDGE,"E1");var subQ2=makeQuery(id+"F0.imprint","INTERSECT",VERTEX,{"derivedFrom":[subQ1,subQ0]});Q1=makeQuery(id+"F0.imprint","IMPRINT",FACE,{"disambiguationData":[TD([[makeQuery(id+"F0.imprint","IMPRINT",EDGE,{"disambiguationData":[TD([[subQ2,-1.0]])],"derivedFrom":subQ1}),-1.0]])]});}
            var Q2;
            {var subQ0=sQuery(id+"F0.wireOp",EDGE,"E4");var subQ1=sQuery(id+"F0.wireOp",EDGE,"E2");var subQ2=makeQuery(id+"F0.imprint","INTERSECT",VERTEX,{"derivedFrom":[subQ1,subQ0]});Q2=makeQuery(id+"F0.imprint","IMPRINT",FACE,{"disambiguationData":[TD([[makeQuery(id+"F0.imprint","IMPRINT",EDGE,{"disambiguationData":[TD([[subQ2,1.0]])],"derivedFrom":subQ1}),-1.0]])]});}
            var Q3;
            {var subQ0=sQuery(id+"F0.wireOp",EDGE,"E4");var subQ1=sQuery(id+"F0.wireOp",EDGE,"E2");var subQ2=makeQuery(id+"F0.imprint","INTERSECT",VERTEX,{"derivedFrom":[subQ1,subQ0]});Q3=makeQuery(id+"F0.imprint","IMPRINT",FACE,{"disambiguationData":[TD([[makeQuery(id+"F0.imprint","IMPRINT",EDGE,{"disambiguationData":[TD([[subQ2,-1.0]])],"derivedFrom":subQ1}),-1.0]])]});}
            var Q4;
            {var subQ0=sQuery(id+"F0.wireOp",EDGE,"E8.left");var subQ1=sQuery(id+"F0.wireOp",EDGE,"E6");var subQ2=makeQuery(id+"F0.imprint","INTERSECT",VERTEX,{"disambiguationData":[OD(1.0)],"derivedFrom":[subQ1,subQ0]});Q4=makeQuery(id+"F0.imprint","IMPRINT",FACE,{"disambiguationData":[TD([[makeQuery(id+"F0.imprint","IMPRINT",EDGE,{"disambiguationData":[TD([[subQ2,-1.0]])],"derivedFrom":subQ1}),1.0]])]});}
            var Q5;
            {var subQ0=sQuery(id+"F0.wireOp",EDGE,"E8.left");var subQ1=sQuery(id+"F0.wireOp",EDGE,"E3");var subQ2=makeQuery(id+"F0.imprint","INTERSECT",VERTEX,{"disambiguationData":[OD(1.0)],"derivedFrom":[subQ1,subQ0]});Q5=makeQuery(id+"F0.imprint","IMPRINT",FACE,{"disambiguationData":[TD([[makeQuery(id+"F0.imprint","IMPRINT",EDGE,{"disambiguationData":[TD([[subQ2,-1.0]])],"derivedFrom":subQ1}),1.0]])]});}
            var Q6;
            {var subQ5=sQuery(id+"F0.wireOp",EDGE,"E8.top");Q6=makeQuery(id+"F0.imprint","IMPRINT",FACE,{"disambiguationData":[TD([[makeQuery(id+"F0.imprint","IMPRINT",EDGE,{"derivedFrom":subQ5}),1.0]])]});}
            extrude(context, id + "F8", {"entities" : qUnion([Q0, Q1, Q2, Q3, Q4, Q5, Q6]), "operationType" : NewBodyOperationType.ADD, "depth" : 25 * mm, "offsetDistance" : 25 * mm, "hasSecondDirection" : true, "secondDirectionOppositeDirection" : true, "secondDirectionDepth" : -13 * mm});
        }
        {
            var Q0;
            Q0=makeQuery(id+"F3.opExtrude","CAP_FACE",FACE,{"disambiguationData":[OSD([sQuery(id+"F0.wireOp",EDGE,"E1"),sQuery(id+"F0.wireOp",EDGE,"E2")])],"isStart":false});
            var sketch = newSketch(context, id + "F9", { "sketchPlane" : qUnion([Q0])});
            skLineSegment(sketch, "E11", {"start": v(0, 69.24) * mm, "end": v(0, -70.43) * mm, "construction": true});
            skLineSegment(sketch, "E12", {"start": v(-70, 61.71) * mm, "end": v(-70, -71.62) * mm, "construction": true});
            skLineSegment(sketch, "E13", {"start": v(50, 61.51) * mm, "end": v(50, -71.62) * mm, "construction": true});
            skLineSegment(sketch, "E14", {"start": v(-59.24, -75) * mm, "end": v(59.23, -75) * mm, "construction": true});
            skLineSegment(sketch, "E15.bottom", {"start": v(-70, -75) * mm, "end": v(-50, -75) * mm});
            skLineSegment(sketch, "E15.top", {"start": v(-70, -70) * mm, "end": v(-50, -70) * mm});
            skLineSegment(sketch, "E15.left", {"start": v(-70, -75) * mm, "end": v(-70, -70) * mm});
            skLineSegment(sketch, "E15.right", {"start": v(-50, -75) * mm, "end": v(-50, -70) * mm});
            skLineSegment(sketch, "E16.bottom", {"start": v(50, -75) * mm, "end": v(30, -75) * mm});
            skLineSegment(sketch, "E16.top", {"start": v(50, -70) * mm, "end": v(30, -70) * mm});
            skLineSegment(sketch, "E16.left", {"start": v(50, -75) * mm, "end": v(50, -70) * mm});
            skLineSegment(sketch, "E16.right", {"start": v(30, -75) * mm, "end": v(30, -70) * mm});
            skLineSegment(sketch, "E17", {"start": v(0, 0) * mm, "end": v(-50, -70) * mm, "construction": true});
            skLineSegment(sketch, "E18", {"start": v(0, 0) * mm, "end": v(30, -70) * mm, "construction": true});
            skLineSegment(sketch, "E19", {"start": v(-50, -75) * mm, "end": v(-4.7, -11.58) * mm});
            skLineSegment(sketch, "E20", {"start": v(30, -75) * mm, "end": v(2.82, -11.58) * mm});
            skLineSegment(sketch, "E21", {"start": v(-53.57, -70) * mm, "end": v(-9.43, -8.2) * mm});
            skLineSegment(sketch, "E22", {"start": v(32.14, -70) * mm, "end": v(6.67, -10.57) * mm});
            skLineSegment(sketch, "E23", {"start": v(-41.55, -53.17) * mm, "end": v(-39.19, -54.86) * mm});
            skLineSegment(sketch, "E24", {"start": v(-39.19, -54.86) * mm, "end": v(-36.82, -56.55) * mm});
            skLineSegment(sketch, "E25", {"start": v(19.6, -50.73) * mm, "end": v(21.4, -49.95) * mm});
            skLineSegment(sketch, "E26", {"start": v(21.4, -49.95) * mm, "end": v(23.22, -49.17) * mm});
            skSolve(sketch);
        }
        {
            var Q0;
            Q0=makeQuery(id+"F9.imprint","IMPRINT",FACE,{"disambiguationData":[TD([[makeQuery(id+"F9.imprint","IMPRINT",EDGE,{"derivedFrom":sQuery(id+"F9.wireOp",EDGE,"E15.bottom")}),1.0]])]});
            var Q1;
            {var subQ1=sQuery(id+"F9.wireOp",EDGE,"E15.right");Q1=makeQuery(id+"F9.imprint","IMPRINT",FACE,{"disambiguationData":[TD([[makeQuery(id+"F9.imprint","IMPRINT",EDGE,{"derivedFrom":subQ1}),-1.0]])]});}
            var Q2;
            {var subQ1=sQuery(id+"F9.wireOp",EDGE,"E23");Q2=makeQuery(id+"F9.imprint","IMPRINT",FACE,{"disambiguationData":[TD([[makeQuery(id+"F9.imprint","IMPRINT",EDGE,{"derivedFrom":subQ1}),1.0]])]});}
            var Q3;
            Q3=makeQuery(id+"F9.imprint","IMPRINT",FACE,{"disambiguationData":[TD([[makeQuery(id+"F9.imprint","IMPRINT",EDGE,{"derivedFrom":sQuery(id+"F9.wireOp",EDGE,"E16.bottom")}),-1.0]])]});
            var Q4;
            {var subQ4=sQuery(id+"F9.wireOp",EDGE,"E16.right");Q4=makeQuery(id+"F9.imprint","IMPRINT",FACE,{"disambiguationData":[TD([[makeQuery(id+"F9.imprint","IMPRINT",EDGE,{"derivedFrom":subQ4}),1.0]])]});}
            var Q5;
            {var subQ1=sQuery(id+"F9.wireOp",EDGE,"E25");Q5=makeQuery(id+"F9.imprint","IMPRINT",FACE,{"disambiguationData":[TD([[makeQuery(id+"F9.imprint","IMPRINT",EDGE,{"derivedFrom":subQ1}),1.0]])]});}
            extrude(context, id + "F10", {"entities" : qUnion([Q0, Q1, Q2, Q3, Q4, Q5]), "operationType" : NewBodyOperationType.ADD, "oppositeDirection" : true, "depth" : 12 * mm, "offsetDistance" : 25 * mm});
        }
        {
            var Q0;
            {var subQ5=sQuery(id+"F0.wireOp",EDGE,"E8.top");Q0=makeQuery(id+"F0.imprint","IMPRINT",FACE,{"disambiguationData":[TD([[makeQuery(id+"F0.imprint","IMPRINT",EDGE,{"derivedFrom":subQ5}),1.0]])]});}
            extrude(context, id + "F11", {"entities" : qUnion([Q0]), "operationType" : NewBodyOperationType.ADD, "depth" : 25 * mm, "offsetDistance" : 25 * mm});
        }
        {
            var Q0;
            Q0=makeQuery(id+"F4.opExtrude","CAP_FACE",FACE,{"disambiguationData":[OSD([sQuery(id+"F0.wireOp",EDGE,"E2"),sQuery(id+"F0.wireOp",EDGE,"E3")])],"isStart":true});
            var sketch = newSketch(context, id + "F12", { "sketchPlane" : qUnion([Q0])});
            skLineSegment(sketch, "E27.bottom", {"start": v(-29, 69.85) * mm, "end": v(-70, 69.85) * mm});
            skLineSegment(sketch, "E27.top", {"start": v(-29, 28.85) * mm, "end": v(-70, 28.85) * mm});
            skLineSegment(sketch, "E27.left", {"start": v(-29, 69.85) * mm, "end": v(-29, 28.85) * mm});
            skLineSegment(sketch, "E27.right", {"start": v(-70, 69.85) * mm, "end": v(-70, 28.85) * mm});
            skLineSegment(sketch, "E28", {"start": v(-49.5, 28.85) * mm, "end": v(-49.5, 69.85) * mm, "construction": true});
            skLineSegment(sketch, "E29", {"start": v(-70, 49.35) * mm, "end": v(-29, 49.35) * mm, "construction": true});
            skCircle(sketch, "E30", {"center": v(-49.5, 49.35) * mm, "radius": 11.35 * mm});
            skCircle(sketch, "E31", {"center": v(-49.5, 49.35) * mm, "radius": 2.5 * mm});
            skCircle(sketch, "E32", {"center": v(-49.5, 49.35) * mm, "radius": 6.5 * mm});
            skLineSegment(sketch, "E33", {"start": v(-49.97, -23.73) * mm, "end": v(-44.97, -23.73) * mm});
            skLineSegment(sketch, "E34", {"start": v(-44.97, -23.73) * mm, "end": v(-44.97, 21.27) * mm});
            skLineSegment(sketch, "E35", {"start": v(-44.97, 21.27) * mm, "end": v(-49.97, 21.27) * mm});
            skLineSegment(sketch, "E36", {"start": v(-49.97, -23.73) * mm, "end": v(-49.97, 21.27) * mm});
            skCircle(sketch, "E37", {"center": v(-65, 64.85) * mm, "radius": 1.55 * mm});
            skCircle(sketch, "E38", {"center": v(-62.17, 62.02) * mm, "radius": 1.55 * mm});
            skCircle(sketch, "E39", {"center": v(-67.83, 67.67) * mm, "radius": 1.55 * mm});
            skLineSegment(sketch, "E40", {"start": v(-49.5, 49.35) * mm, "end": v(-65, 64.85) * mm, "construction": true});
            skLineSegment(sketch, "E41", {"start": v(-63.21, 63.06) * mm, "end": v(-65, 64.85) * mm, "construction": true});
            skLineSegment(sketch, "E42", {"start": v(-65, 64.85) * mm, "end": v(-71.97, 57.88) * mm, "construction": true});
            skLineSegment(sketch, "E43", {"start": v(-66.66, 68.7) * mm, "end": v(-61.08, 63.11) * mm});
            skLineSegment(sketch, "E44", {"start": v(-68.9, 66.55) * mm, "end": v(-63.27, 60.92) * mm});
            skCircle(sketch, "E45.1.0.0", {"center": v(-36.83, 67.67) * mm, "radius": 1.55 * mm});
            skCircle(sketch, "E45.1.0.1", {"center": v(-34, 64.85) * mm, "radius": 1.55 * mm});
            skCircle(sketch, "E45.1.0.2", {"center": v(-31.17, 62.02) * mm, "radius": 1.55 * mm});
            skLineSegment(sketch, "E45.1.0.3", {"start": v(-35.66, 68.7) * mm, "end": v(-30.08, 63.11) * mm});
            skLineSegment(sketch, "E45.1.0.4", {"start": v(-37.9, 66.55) * mm, "end": v(-32.27, 60.92) * mm});
            skLineSegment(sketch, "E45.direction1", {"start": v(-67.83, 67.67) * mm, "end": v(-36.83, 67.67) * mm, "construction": true});
            skCircle(sketch, "E46.1.0.0", {"center": v(-67.83, 36.67) * mm, "radius": 1.55 * mm});
            skCircle(sketch, "E46.1.0.1", {"center": v(-65, 33.85) * mm, "radius": 1.55 * mm});
            skCircle(sketch, "E46.1.0.2", {"center": v(-62.17, 31.02) * mm, "radius": 1.55 * mm});
            skLineSegment(sketch, "E46.1.0.3", {"start": v(-68.9, 35.55) * mm, "end": v(-63.27, 29.92) * mm});
            skLineSegment(sketch, "E46.1.0.4", {"start": v(-66.66, 37.7) * mm, "end": v(-61.08, 32.11) * mm});
            skLineSegment(sketch, "E46.direction1", {"start": v(-67.83, 67.67) * mm, "end": v(-67.83, 36.67) * mm, "construction": true});
            skCircle(sketch, "E47.1.0.0", {"center": v(-36.83, 36.67) * mm, "radius": 1.55 * mm});
            skCircle(sketch, "E47.1.0.1", {"center": v(-34, 33.85) * mm, "radius": 1.55 * mm});
            skCircle(sketch, "E47.1.0.2", {"center": v(-31.17, 31.02) * mm, "radius": 1.55 * mm});
            skLineSegment(sketch, "E47.1.0.3", {"start": v(-35.66, 37.7) * mm, "end": v(-30.08, 32.11) * mm});
            skLineSegment(sketch, "E47.1.0.4", {"start": v(-37.9, 35.55) * mm, "end": v(-32.27, 29.92) * mm});
            skLineSegment(sketch, "E47.direction1", {"start": v(-67.83, 36.67) * mm, "end": v(-36.83, 36.67) * mm, "construction": true});
            skSolve(sketch);
        }
        {
            var Q0;
            Q0=makeQuery(id+"F12.imprint","IMPRINT",FACE,{"disambiguationData":[TD([[makeQuery(id+"F12.imprint","IMPRINT",EDGE,{"derivedFrom":sQuery(id+"F12.wireOp",EDGE,"E31")}),-1.0]])]});
            extrude(context, id + "F13", {"entities" : qUnion([Q0]), "oppositeDirection" : true, "depth" : 25 * mm, "offsetDistance" : 25 * mm});
        }
        {
            var Q0;
            {var subQ4=sQuery(id+"F12.wireOp",EDGE,"E27.bottom");var subQ6=sQuery(id+"F12.wireOp",EDGE,"E27.left");var subQ7=makeQuery(id+"F12.imprint","INTERSECT",VERTEX,{"derivedFrom":[subQ4,subQ6]});Q0=makeQuery(id+"F12.imprint","IMPRINT",FACE,{"disambiguationData":[TD([[makeQuery(id+"F12.imprint","IMPRINT",EDGE,{"disambiguationData":[TD([[subQ7,-1.0]])],"derivedFrom":subQ4}),1.0]])]});}
            extrude(context, id + "F14", {"entities" : qUnion([Q0]), "operationType" : NewBodyOperationType.REMOVE, "oppositeDirection" : true, "depth" : 2 * mm, "offsetDistance" : 25 * mm});
        }
        {
            var Q0;
            {var subQ0=sQuery(id+"F0.wireOp",EDGE,"E3");Q0=makeQuery(id+"F14.boolean.opBoolean","SPLIT",FACE,{"disambiguationData":[TD([makeQuery(id+"F14.opExtrude","SWEPT_FACE",FACE,{"disambiguationData":[OSD([sQuery(id+"F12.wireOp",EDGE,"E30")])]})])],"derivedFrom":makeQuery(id+"F4.opExtrude","CAP_FACE",FACE,{"disambiguationData":[OSD([sQuery(id+"F0.wireOp",EDGE,"E2"),subQ0])],"isStart":true})});}
            extrude(context, id + "F15", {"entities" : qUnion([Q0]), "operationType" : NewBodyOperationType.REMOVE, "endBound" : BoundingType.UP_TO_NEXT, "oppositeDirection" : true, "depth" : 25 * mm, "offsetDistance" : 25 * mm});
        }
    });
